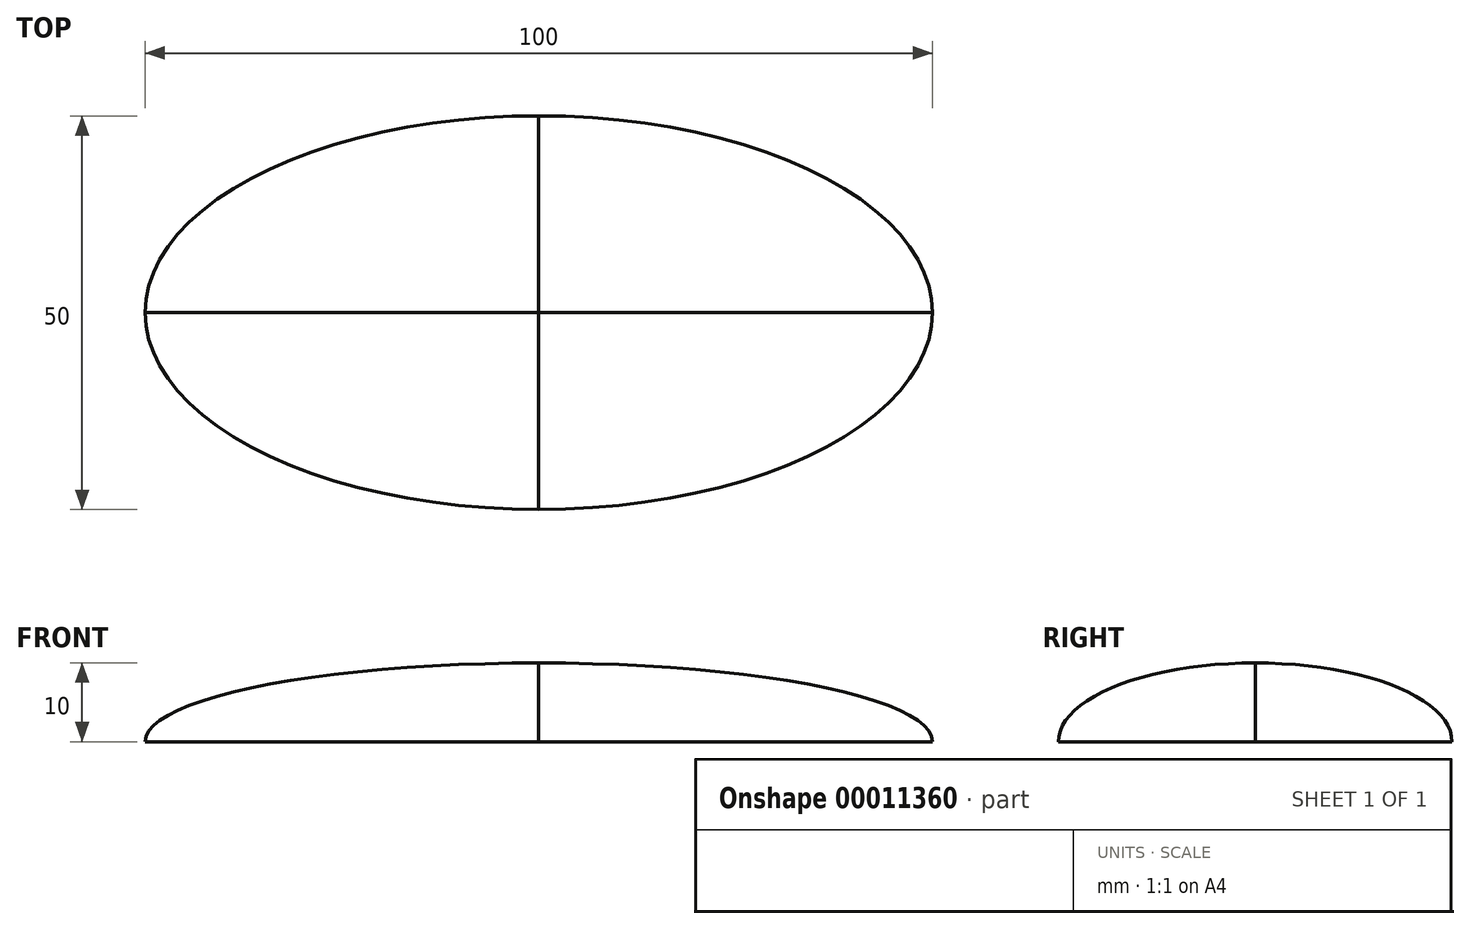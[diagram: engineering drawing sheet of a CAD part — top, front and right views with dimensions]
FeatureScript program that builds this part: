
annotation { "Feature Type Name" : "Feature", "Feature Type Description" : "" }
export const myFeature = defineFeature(function(context is Context, id is Id, definition is map)
    precondition{}
    {
        {
            var Q0;
            Q0=qCreatedBy(makeId("Top.planeOp"),FACE);
            var sketch = newSketch(context, id + "F0", { "sketchPlane" : qUnion([Q0])});
            skEllipticalArc(sketch, "E0", {});
            skLineSegment(sketch, "E1", {"start": v(0, 0) * mm, "end": v(50, 0) * mm, "construction": true});
            skLineSegment(sketch, "E2", {"start": v(0, 0) * mm, "end": v(0, 25) * mm, "construction": true});
            const initialGuessF0  = {"E0": [0, 0, 1, 0, 0.05, 0.025, 0, 1.5707963267948966]};
            skSetInitialGuess(sketch, initialGuessF0);
            skSolve(sketch);
        }
        {
            var Q0;
            Q0=qCreatedBy(makeId("Front.planeOp"),FACE);
            var sketch = newSketch(context, id + "F1", { "sketchPlane" : qUnion([Q0])});
            skLineSegment(sketch, "E3", {"start": v(0, 0) * mm, "end": v(0, 10) * mm});
            skLineSegment(sketch, "E4", {"start": v(50, 0) * mm, "end": v(0, 0) * mm});
            skEllipticalArc(sketch, "E5", {});
            const initialGuessF1  = {"E5": [0, 0, 0, 1, 0.01, 0.05, 4.71238898038469, 6.283185307179586]};
            skSetInitialGuess(sketch, initialGuessF1);
            skSolve(sketch);
        }
        {
            var Q0;
            Q0=qCreatedBy(makeId("Right.planeOp"),FACE);
            var sketch = newSketch(context, id + "F2", { "sketchPlane" : qUnion([Q0])});
            skLineSegment(sketch, "E6", {"start": v(0, 0) * mm, "end": v(0, 10) * mm});
            skLineSegment(sketch, "E7", {"start": v(25, 0) * mm, "end": v(0, 0) * mm});
            skEllipticalArc(sketch, "E8", {});
            const initialGuessF2  = {"E8": [0, 0, 0, 1, 0.01, 0.025, 4.71238898038469, 6.283185307179586]};
            skSetInitialGuess(sketch, initialGuessF2);
            skSolve(sketch);
        }
        {
            var Q0;
            Q0=makeQuery(id+"F1.imprint","IMPRINT",FACE,{"disambiguationData":[TD([[makeQuery(id+"F1.imprint","IMPRINT",EDGE,{"derivedFrom":sQuery(id+"F1.wireOp",EDGE,"E3")}),-1.0]])]});
            var Q1;
            Q1=makeQuery(id+"F2.imprint","IMPRINT",FACE,{"disambiguationData":[TD([[makeQuery(id+"F2.imprint","IMPRINT",EDGE,{"derivedFrom":sQuery(id+"F2.wireOp",EDGE,"E6")}),-1.0]])]});
            var Q2;
            Q2=sQuery(id+"F0.wireOp",EDGE,"E0");
            var Q3;
            Q3=sQuery(id+"F1.wireOp",VERTEX,"E5.start");
            var Q4;
            Q4=sQuery(id+"F2.wireOp",VERTEX,"E8.start");
            loft(context, id + "F3", {"addGuides" : true, "sheetProfilesArray" : [{ "sheetProfileEntities" : qUnion([Q0]) }, { "sheetProfileEntities" : qUnion([Q1]) }], "guidesArray" : [{ "guideEntities" : qUnion([Q2]), "guideDerivativeType" : LoftGuideDerivativeType.DEFAULT, "guideDerivativeMagnitude" : 1 }], "matchConnections" : true, "connections" : [{ "connectionEntities" : qUnion([Q3, Q4]), "connectionEdgeQueries" : qUnion([]), "connectionEdgeParameters" : [] }]});
        }
        {
            var Q0;
            Q0=makeQuery(id+"F3.opLoft","SWEPT_BODY",BODY,{"disambiguationData":[OSD([sQuery(id+"F0.wireOp",EDGE,"E0"),makeQuery(id+"F1.imprint","IMPRINT",FACE,{"disambiguationData":[TD([[makeQuery(id+"F1.imprint","IMPRINT",EDGE,{"derivedFrom":sQuery(id+"F1.wireOp",EDGE,"E3")}),-1.0]])]}),makeQuery(id+"F2.imprint","IMPRINT",FACE,{"disambiguationData":[TD([[makeQuery(id+"F2.imprint","IMPRINT",EDGE,{"derivedFrom":sQuery(id+"F2.wireOp",EDGE,"E6")}),-1.0]])]})])]});
            var Q1;
            Q1=makeQuery(id+"F3.opLoft","CAP_FACE",FACE,{"disambiguationData":[OSD([makeQuery(id+"F2.imprint","IMPRINT",FACE,{"disambiguationData":[TD([[makeQuery(id+"F2.imprint","IMPRINT",EDGE,{"derivedFrom":sQuery(id+"F2.wireOp",EDGE,"E6")}),-1.0]])]})])],"isStart":true});
            mirror(context, id + "F4", {"operationType" : NewBodyOperationType.ADD, "entities" : qUnion([Q0]), "mirrorPlane" : qUnion([Q1])});
        }
        {
            var Q0;
            Q0=makeQuery(id+"F3.opLoft","SWEPT_BODY",BODY,{"disambiguationData":[OSD([sQuery(id+"F0.wireOp",EDGE,"E0"),makeQuery(id+"F1.imprint","IMPRINT",FACE,{"disambiguationData":[TD([[makeQuery(id+"F1.imprint","IMPRINT",EDGE,{"derivedFrom":sQuery(id+"F1.wireOp",EDGE,"E3")}),-1.0]])]}),makeQuery(id+"F2.imprint","IMPRINT",FACE,{"disambiguationData":[TD([[makeQuery(id+"F2.imprint","IMPRINT",EDGE,{"derivedFrom":sQuery(id+"F2.wireOp",EDGE,"E6")}),-1.0]])]})])]});
            var Q1;
            {var subQ0=makeQuery(id+"F3.opLoft","CAP_FACE",FACE,{"disambiguationData":[OSD([makeQuery(id+"F1.imprint","IMPRINT",FACE,{"disambiguationData":[TD([[makeQuery(id+"F1.imprint","IMPRINT",EDGE,{"derivedFrom":sQuery(id+"F1.wireOp",EDGE,"E3")}),-1.0]])]})])],"isStart":true});Q1=makeQuery(id+"F4.boolean.opBoolean","MERGE",FACE,{"derivedFrom":[subQ0,makeQuery(id+"F4.opPattern","COPY",FACE,{"derivedFrom":subQ0,"instanceName":"1"})]});}
            mirror(context, id + "F5", {"operationType" : NewBodyOperationType.ADD, "entities" : qUnion([Q0]), "mirrorPlane" : qUnion([Q1])});
        }
    });
